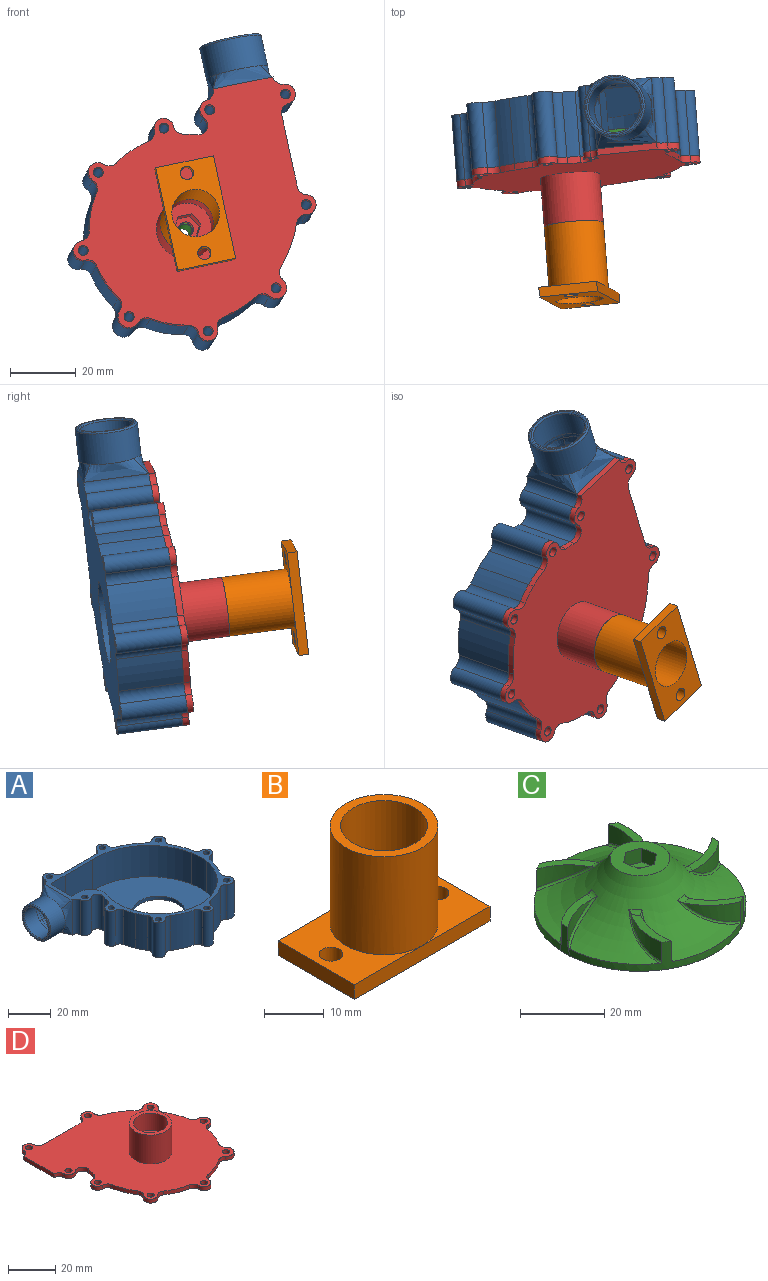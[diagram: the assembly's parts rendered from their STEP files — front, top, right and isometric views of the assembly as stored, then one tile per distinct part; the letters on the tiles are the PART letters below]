
ASSEMBLY  parts=4 mates=3
PART A: 83 faces, bbox 89.8x76.4x20.8 mm
  f0: cylinder r=29.1mm len=20mm, axis (0,0,-1), area 123.2mm2, adj f1,f7,f16,f63
  f1: cylinder r=29.1mm len=20mm, axis (0,0,-1), area 116.2mm2, adj f0,f7,f16,f54
  f2: cylinder r=29.1mm len=20mm, axis (0,0,-1), area 242.2mm2, adj f7,f16,f50,f56
  f3: cylinder r=29.1mm len=20mm, axis (0,0,-1), area 236.9mm2, adj f7,f16,f46,f52
  f4: cylinder r=38.12mm len=20mm, axis (0,0,-1), area 241.8mm2, adj f7,f11,f16,f40
  f5: cylinder r=38.12mm len=20mm, axis (0,0,-1), area 292.6mm2, adj f7,f16,f36,f42
  f6: cylinder r=8.51mm len=18mm, axis (0,0,-1), area 233.2mm2, adj f7,f26,f27,f28,f29,f30
  f7: plane 76.42x75.05mm, normal (0,0,1), area 691.8mm2, adj f0,f1,f2,f3,f4,f5,f6,f8
  f8: cylinder r=29.1mm len=20mm, axis (0,0,-1), area 80mm2, adj f7,f15,f16,f61
  f9: cylinder r=29.1mm len=20mm, axis (0,0,-1), area 235.3mm2, adj f7,f10,f16,f48
  f10: cylinder r=3mm len=20mm, axis (0,0,-1), area 83.6mm2, adj f7,f9,f16,f44
  f11: cylinder r=3mm len=20mm, axis (0,0,-1), area 84.8mm2, adj f4,f7,f16,f44
  f12: cylinder r=38.12mm len=20mm, axis (0,0,-1), area 85.1mm2, adj f7,f13,f16,f38
  f13: plane 20x18.02mm, normal (0,1,0), area 360.4mm2, adj f7,f12,f16,f33
  f14: plane 20x0.02mm, normal (0,-1,0), area 0.4mm2, adj f7,f16,f58,f66
  f15: cylinder r=3mm len=20mm, axis (0,0,-1), area 156mm2, adj f7,f8,f16,f59
  f16: plane 76.42x75.05mm, normal (0,0,-1), area 3092.9mm2, adj f0,f1,f2,f3,f4,f5,f8,f9
  f17: cylinder r=27.1mm len=19.22mm, axis (0,0,-1), area 354mm2, adj f7,f18,f27,f28
  f18: cylinder r=27.1mm len=51.79mm, axis (0,0,-1), area 1258.4mm2, adj f7,f17,f19,f28
  f19: cylinder r=5mm len=18mm, axis (0,0,-1), area 0.8mm2, adj f7,f18,f20,f28
  f20: cylinder r=24.78mm len=18mm, axis (0,0,-1), area 178.9mm2, adj f7,f19,f21,f28
  f21: cylinder r=5mm len=18mm, axis (0,0,-1), area 3.9mm2, adj f7,f20,f22,f28
  f22: cylinder r=36.12mm len=36.86mm, axis (0,0,-1), area 918mm2, adj f7,f21,f23,f28
  f23: plane 18.05x18mm, normal (0,-1,0), area 324.9mm2, adj f7,f22,f24,f28
  f24: plane 18x9.91mm, normal (0.01,-1,0), area 178.4mm2, adj f7,f23,f25,f28
  f25: plane 18x14.36mm, normal (1,0,0), area 29.1mm2, adj f7,f24,f26,f28,f30,f31
  f26: plane 3.82x2mm, normal (-0.08,1,0), area 7.7mm2, adj f6,f7,f25,f30
  f27: cylinder r=5mm len=18mm, axis (0,0,-1), area 7.9mm2, adj f6,f7,f17,f28
  f28: plane 67.53x61.45mm, normal (0,0,1), area 2433mm2, adj f6,f17,f18,f19,f20,f21,f22,f23
  f29: plane 16x9.59mm, normal (0,1,0), area 153.4mm2, adj f6,f28,f30,f73
  f30: plane 14.56x9.59mm, normal (0,0,-1), area 31.9mm2, adj f6,f25,f26,f29,f31,f72
  f31: plane 16x2mm, normal (0,-1,0), area 32mm2, adj f25,f28,f30,f71
  f32: cylinder r=3mm len=20mm, axis (0,0,-1), area 88.8mm2, adj f7,f16,f34,f68
  f33: cylinder r=3mm len=20mm, axis (0,0,-1), area 89.2mm2, adj f7,f13,f16,f34
  f34: cylinder r=3mm len=20mm, axis (0,0,-1), area 179.5mm2, adj f7,f16,f32,f33
  f35: cylinder r=1.5mm len=20mm, axis (0,0,-1), area 188.5mm2, adj f7,f16
  f36: cylinder r=3mm len=20mm, axis (0,0,-1), area 84.2mm2, adj f5,f7,f16,f37
  f37: cylinder r=3mm len=20mm, axis (0,0,-1), area 186mm2, adj f7,f16,f36,f38
  f38: cylinder r=3mm len=20mm, axis (0,0,-1), area 84.2mm2, adj f7,f12,f16,f37
  f39: cylinder r=1.5mm len=20mm, axis (0,0,-1), area 188.5mm2, adj f7,f16
  f40: cylinder r=3mm len=20mm, axis (0,0,-1), area 84.7mm2, adj f4,f7,f16,f41
  f41: cylinder r=3.26mm len=20mm, axis (0,0,-1), area 203.7mm2, adj f7,f16,f40,f42
  f42: cylinder r=3mm len=20mm, axis (0,0,-1), area 84.7mm2, adj f5,f7,f16,f41
  f43: cylinder r=1.5mm len=20mm, axis (0,0,-1), area 188.5mm2, adj f7,f16
  f44: cylinder r=3mm len=20mm, axis (0,0,-1), area 191mm2, adj f7,f10,f11,f16
  f45: cylinder r=1.5mm len=20mm, axis (0,0,-1), area 188.5mm2, adj f7,f16
  f46: cylinder r=3mm len=20mm, axis (0,0,-1), area 83.6mm2, adj f3,f7,f16,f47
  f47: cylinder r=3.38mm len=20mm, axis (0,0,-1), area 215.1mm2, adj f7,f16,f46,f48
  f48: cylinder r=3mm len=20mm, axis (0,0,-1), area 83.6mm2, adj f7,f9,f16,f47
  f49: cylinder r=1.5mm len=20mm, axis (0,0,-1), area 188.5mm2, adj f7,f16
  f50: cylinder r=3mm len=20mm, axis (0,0,-1), area 83.6mm2, adj f2,f7,f16,f51
  f51: cylinder r=3mm len=20mm, axis (0,0,-1), area 189.8mm2, adj f7,f16,f50,f52
  f52: cylinder r=3mm len=20mm, axis (0,0,-1), area 83.6mm2, adj f3,f7,f16,f51
  f53: cylinder r=1.5mm len=20mm, axis (0,0,-1), area 188.5mm2, adj f7,f16
  f54: cylinder r=3mm len=20mm, axis (0,0,-1), area 83.6mm2, adj f1,f7,f16,f55
  f55: cylinder r=3mm len=20mm, axis (0,0,-1), area 189.8mm2, adj f7,f16,f54,f56
  f56: cylinder r=3mm len=20mm, axis (0,0,-1), area 83.6mm2, adj f2,f7,f16,f55
  f57: cylinder r=1.5mm len=20mm, axis (0,0,-1), area 188.5mm2, adj f7,f16
  f58: cylinder r=3mm len=20mm, axis (0,0,-1), area 89.2mm2, adj f7,f14,f16,f59
  f59: cylinder r=3mm len=20mm, axis (0,0,-1), area 131.5mm2, adj f7,f15,f16,f58
  f60: cylinder r=1.5mm len=20mm, axis (0,0,-1), area 188.5mm2, adj f7,f16
  f61: cylinder r=3mm len=20mm, axis (0,0,-1), area 83.6mm2, adj f7,f8,f16,f62
  f62: cylinder r=3mm len=20mm, axis (0,0,-1), area 189.8mm2, adj f7,f16,f61,f63
  f63: cylinder r=3mm len=20mm, axis (0,0,-1), area 83.6mm2, adj f0,f7,f16,f62
  f64: cylinder r=1.5mm len=20mm, axis (0,0,-1), area 188.5mm2, adj f7,f16
  f65: cylinder r=12.5mm len=25mm, axis (0,0,-1), area 157.1mm2, adj f16,f28
  f66: bspline ~20x4.7mm, area 84.7mm2, adj f14,f67,f69,f74
  f67: bspline ~18.52x4.79mm, area 86.6mm2, adj f7,f66,f68,f74
  f68: bspline ~20x4.79mm, area 85.6mm2, adj f32,f67,f69,f74
  f69: bspline ~18.52x4.79mm, area 81.8mm2, adj f16,f66,f68,f74
  f70: bspline ~14.52x4.78mm, area 65.1mm2, adj f28,f71,f73,f79
  f71: bspline ~16x4.78mm, area 69.3mm2, adj f31,f70,f72,f80
  f72: bspline ~14.52x4.78mm, area 66.7mm2, adj f30,f71,f73,f78
  f73: bspline ~16x4.71mm, area 68.3mm2, adj f29,f70,f72,f77
  f74: cylinder r=9.5mm len=19mm, axis (1,0,0), area 567.1mm2, adj f66,f67,f68,f69,f82
  f75: plane 18x18mm, normal (-1,0,0), area 27.5mm2, adj f81,f82
  f76: cylinder r=8mm len=16mm, axis (-1,0,0), area 399mm2, adj f77,f78,f79,f80,f81
  f77: bspline ~12.11x2.96mm, area 20.1mm2, adj f73,f76,f78,f79
  f78: bspline ~12.11x2.96mm, area 20.2mm2, adj f72,f76,f77,f80
  f79: bspline ~12.11x2.96mm, area 20.2mm2, adj f70,f76,f77,f80
  f80: bspline ~12.11x2.96mm, area 20.2mm2, adj f71,f76,f78,f79
  f81: torus R=8.5mm, axis (1,0,0), area 40.4mm2, adj f75,f76
  f82: torus R=9mm, axis (1,0,0), area 46mm2, adj f74,f75
PART B: 12 faces, bbox 32x18x23 mm
  f0: cylinder r=7.25mm len=23mm, axis (0,0,-1), area 1047.7mm2, adj f2,f9
  f1: cylinder r=9mm len=20mm, axis (0,0,-1), area 1131mm2, adj f2,f3,f6
  f2: plane 18x18mm, normal (0,0,1), area 89.3mm2, adj f0,f1
  f3: plane 18x16mm, normal (0,0,1), area 148.2mm2, adj f1,f5,f7,f8,f11
  f4: plane 18x3mm, normal (-1,0,0), area 54mm2, adj f6,f7,f8,f9
  f5: plane 18x3mm, normal (1,0,0), area 54mm2, adj f3,f7,f8,f9
  f6: plane 18x16mm, normal (0,0,1), area 148.2mm2, adj f1,f4,f7,f8,f10
  f7: plane 32x3mm, normal (0,1,0), area 96mm2, adj f3,f4,f5,f6,f9
  f8: plane 32x3mm, normal (0,-1,0), area 96mm2, adj f3,f4,f5,f6,f9
  f9: plane 32x18mm, normal (0,0,-1), area 385.7mm2, adj f0,f4,f5,f7,f8,f10,f11
  f10: cylinder r=2mm len=4mm, axis (0,0,-1), area 37.7mm2, adj f6,f9
  f11: cylinder r=2mm len=4mm, axis (0,0,-1), area 37.7mm2, adj f3,f9
PART C: 48 faces, bbox 61.1x61.1x26.7 mm
  f0: cylinder r=2.1mm len=11mm, axis (0,0,-1), area 145.1mm2, adj f3,f29
  f1: torus R=29.21mm, axis (0,0,-1), area 1865.6mm2, adj f2,f4,f30,f31,f32,f33,f34,f35
  f2: plane 14.2x14.2mm, normal (0,0,1), area 112.2mm2, adj f1,f23,f24,f25,f26,f27,f28
  f3: plane 50.2x50.2mm, normal (0,0,-1), area 1965.4mm2, adj f0,f4
  f4: cylinder r=25.1mm len=50.2mm, axis (0,0,-1), area 400.2mm2, adj f1,f3,f5,f6,f7,f8,f9,f10
  f5: cylinder r=18mm len=12.05mm, axis (0,0,-1), area 35.5mm2, adj f4,f7,f39
  f6: cylinder r=18mm len=13.06mm, axis (0,0,-1), area 49.9mm2, adj f4,f7,f38,f46
  f7: plane 12.88x6.41mm, normal (0,0,1), area 27.6mm2, adj f4,f5,f6,f39,f46
  f8: plane 14.32x4.63mm, normal (0,0,1), area 27.6mm2, adj f4,f9,f10,f37,f45
  f9: cylinder r=18mm len=13.33mm, axis (0,0,-1), area 49.9mm2, adj f4,f8,f36,f45
  f10: cylinder r=18mm len=12.56mm, axis (0,0,-1), area 35.5mm2, adj f4,f8,f37
  f11: plane 12.88x6.41mm, normal (0,0,1), area 27.6mm2, adj f4,f12,f13,f33,f43
  f12: cylinder r=18mm len=12.05mm, axis (0,0,-1), area 35.5mm2, adj f4,f11,f33
  f13: cylinder r=18mm len=13.06mm, axis (0,0,-1), area 49.9mm2, adj f4,f11,f32,f43
  f14: cylinder r=18mm len=13.33mm, axis (0,0,-1), area 49.9mm2, adj f4,f16,f30,f42
  f15: cylinder r=18mm len=12.56mm, axis (0,0,-1), area 35.5mm2, adj f4,f16,f31
  f16: plane 14.32x4.63mm, normal (0,0,1), area 27.6mm2, adj f4,f14,f15,f31,f42
  f17: cylinder r=18mm len=10.03mm, axis (0,0,-1), area 49.9mm2, adj f4,f19,f34,f44
  f18: cylinder r=18mm len=9.7mm, axis (0,0,-1), area 35.5mm2, adj f4,f19,f35
  f19: plane 11.94x9.52mm, normal (0,0,1), area 27.6mm2, adj f4,f17,f18,f35,f44
  f20: cylinder r=18mm len=9.7mm, axis (0,0,-1), area 35.5mm2, adj f4,f22,f40
  f21: cylinder r=18mm len=10.03mm, axis (0,0,-1), area 49.9mm2, adj f4,f22,f41,f47
  f22: plane 11.94x9.52mm, normal (0,0,1), area 27.6mm2, adj f4,f20,f21,f40,f47
  f23: plane 4x3.93mm, normal (0.36,0.93,0), area 16.9mm2, adj f2,f24,f28,f29
  f24: plane 4x3.28mm, normal (-0.63,0.78,0), area 16.9mm2, adj f2,f23,f25,f29
  f25: plane 4.16x4mm, normal (-0.99,-0.15,0), area 16.9mm2, adj f2,f24,f26,f29
  f26: plane 4x3.93mm, normal (-0.36,-0.93,0), area 16.9mm2, adj f2,f25,f27,f29
  f27: plane 4x3.28mm, normal (0.63,-0.78,0), area 16.9mm2, adj f2,f26,f28,f29
  f28: plane 4.16x4mm, normal (0.99,0.15,0), area 16.9mm2, adj f2,f23,f27,f29
  f29: plane 8.33x7.86mm, normal (0,0,1), area 32.3mm2, adj f0,f23,f24,f25,f26,f27,f28
  f30: bspline ~17.28x8.18mm, area 11mm2, adj f1,f4,f14,f42
  f31: bspline ~16.64x8.2mm, area 13.1mm2, adj f1,f4,f15,f16,f42
  f32: bspline ~16.34x8.08mm, area 11mm2, adj f1,f4,f13,f43
  f33: bspline ~16.1x8.2mm, area 13.1mm2, adj f1,f4,f11,f12,f43
  f34: bspline ~12.58x12.41mm, area 11mm2, adj f1,f4,f17,f44
  f35: bspline ~12.7x10.93mm, area 13.1mm2, adj f1,f4,f18,f19,f44
  f36: bspline ~17.28x8.18mm, area 11mm2, adj f1,f4,f9,f45
  f37: bspline ~16.64x8.2mm, area 13.1mm2, adj f1,f4,f8,f10,f45
  f38: bspline ~16.34x8.08mm, area 11mm2, adj f1,f4,f6,f46
  f39: bspline ~16.1x8.2mm, area 13.1mm2, adj f1,f4,f5,f7,f46
  f40: bspline ~12.7x10.93mm, area 13.1mm2, adj f1,f4,f20,f22,f47
  f41: bspline ~12.58x12.41mm, area 11mm2, adj f1,f4,f21,f47
  f42: torus R=13.36mm, axis (0,0,1), area 4mm2, adj f1,f14,f16,f30,f31
  f43: torus R=13.36mm, axis (0,0,1), area 4mm2, adj f1,f11,f13,f32,f33
  f44: torus R=13.36mm, axis (0,0,1), area 4mm2, adj f1,f17,f19,f34,f35
  f45: torus R=13.36mm, axis (0,0,1), area 4mm2, adj f1,f8,f9,f36,f37
  f46: torus R=13.36mm, axis (0,0,1), area 4mm2, adj f1,f6,f7,f38,f39
  f47: torus R=13.36mm, axis (0,0,1), area 4mm2, adj f1,f21,f22,f40,f41
PART D: 62 faces, bbox 75.1x76.4x17 mm
  f0: cylinder r=2.25mm len=4.5mm, axis (0,0,1), area 28.3mm2, adj f50,f61
  f1: cylinder r=29.1mm len=5.89mm, axis (0,0,-1), area 12.3mm2, adj f2,f47,f49,f50
  f2: cylinder r=29.1mm len=5.13mm, axis (0,0,-1), area 11.6mm2, adj f1,f3,f49,f50
  f3: cylinder r=3mm len=3.83mm, axis (0,0,-1), area 8.4mm2, adj f2,f4,f49,f50
  f4: cylinder r=3mm len=5.17mm, axis (0,0,-1), area 19mm2, adj f3,f5,f49,f50
  f5: cylinder r=3mm len=3.84mm, axis (0,0,-1), area 8.4mm2, adj f4,f6,f49,f50
  f6: cylinder r=29.1mm len=11.07mm, axis (0,0,-1), area 24.2mm2, adj f5,f7,f49,f50
  f7: cylinder r=3mm len=2.99mm, axis (0,0,-1), area 8.4mm2, adj f6,f8,f49,f50
  f8: cylinder r=3mm len=6mm, axis (0,0,-1), area 19mm2, adj f7,f9,f49,f50
  f9: cylinder r=3mm len=2.97mm, axis (0,0,-1), area 8.4mm2, adj f8,f10,f49,f50
  f10: cylinder r=29.1mm len=10.9mm, axis (0,0,-1), area 23.7mm2, adj f9,f11,f49,f50
  f11: cylinder r=3mm len=3.83mm, axis (0,0,-1), area 8.4mm2, adj f10,f12,f49,f50
  f12: cylinder r=3.38mm len=5.83mm, axis (0,0,-1), area 21.5mm2, adj f11,f13,f49,f50
  f13: cylinder r=3mm len=3.82mm, axis (0,0,-1), area 8.4mm2, adj f12,f14,f49,f50
  f14: cylinder r=29.1mm len=10.86mm, axis (0,0,-1), area 23.5mm2, adj f13,f15,f49,f50
  f15: cylinder r=3mm len=2.95mm, axis (0,0,-1), area 8.4mm2, adj f14,f16,f49,f50
  f16: cylinder r=3mm len=6mm, axis (0,0,-1), area 19.1mm2, adj f15,f17,f49,f50
  f17: cylinder r=3mm len=3.07mm, axis (0,0,-1), area 8.5mm2, adj f16,f18,f49,f50
  f18: cylinder r=38.12mm len=11.28mm, axis (0,0,-1), area 24.2mm2, adj f17,f19,f49,f50
  f19: cylinder r=3mm len=3.82mm, axis (0,0,-1), area 8.5mm2, adj f18,f20,f49,f50
  f20: cylinder r=3.26mm len=5.8mm, axis (0,0,-1), area 20.4mm2, adj f19,f21,f49,f50
  f21: cylinder r=3mm len=3.89mm, axis (0,0,-1), area 8.5mm2, adj f20,f22,f49,f50
  f22: cylinder r=38.12mm len=12.34mm, axis (0,0,-1), area 29.3mm2, adj f21,f23,f49,f50
  f23: cylinder r=3mm len=3.39mm, axis (0,0,-1), area 8.4mm2, adj f22,f24,f49,f50
  f24: cylinder r=3mm len=5.91mm, axis (0,0,-1), area 18.6mm2, adj f23,f25,f49,f50
  f25: cylinder r=3mm len=3.13mm, axis (0,0,-1), area 8.4mm2, adj f24,f26,f49,f50
  f26: cylinder r=38.12mm len=4.25mm, axis (0,0,-1), area 8.5mm2, adj f25,f27,f49,f50
  f27: plane 18.02x2mm, normal (0,1,0), area 36mm2, adj f26,f28,f49,f50
  f28: cylinder r=3mm len=2.99mm, axis (0,0,-1), area 8.9mm2, adj f27,f29,f49,f50
  f29: cylinder r=3mm len=5.98mm, axis (0,0,-1), area 18mm2, adj f28,f30,f49,f50
  f30: cylinder r=3mm len=2.92mm, axis (0,0,-1), area 8.9mm2, adj f29,f31,f49,f50
  f31: plane 18.52x2mm, normal (-1,0,0), area 37mm2, adj f30,f32,f49,f50
  f32: plane 2x0.02mm, normal (0,-1,0), area 0mm2, adj f31,f33,f49,f50
  f33: cylinder r=3mm len=2.99mm, axis (0,0,-1), area 8.9mm2, adj f32,f34,f49,f50
  f34: cylinder r=3mm len=4.93mm, axis (0,0,-1), area 13.1mm2, adj f33,f35,f49,f50
  f35: cylinder r=3mm len=4.94mm, axis (0,0,-1), area 15.6mm2, adj f34,f36,f49,f50
  f36: cylinder r=29.1mm len=3.87mm, axis (0,0,-1), area 8mm2, adj f35,f37,f49,f50
  f37: cylinder r=3mm len=2.98mm, axis (0,0,-1), area 8.4mm2, adj f36,f38,f49,f50
  f38: cylinder r=3mm len=6mm, axis (0,0,-1), area 19mm2, adj f37,f47,f49,f50
  f39: cylinder r=1.5mm len=3mm, axis (0,0,-1), area 18.8mm2, adj f49,f50
  f40: cylinder r=1.5mm len=3mm, axis (0,0,-1), area 18.8mm2, adj f49,f50
  f41: cylinder r=1.5mm len=3mm, axis (0,0,-1), area 18.8mm2, adj f49,f50
  f42: cylinder r=1.5mm len=3mm, axis (0,0,-1), area 18.8mm2, adj f49,f50
  f43: cylinder r=1.5mm len=3mm, axis (0,0,-1), area 18.8mm2, adj f49,f50
  f44: cylinder r=1.5mm len=3mm, axis (0,0,-1), area 18.8mm2, adj f49,f50
  f45: cylinder r=1.5mm len=3mm, axis (0,0,-1), area 18.8mm2, adj f49,f50
  f46: cylinder r=1.5mm len=3mm, axis (0,0,-1), area 18.8mm2, adj f49,f50
  f47: cylinder r=3mm len=2.98mm, axis (0,0,-1), area 8.4mm2, adj f1,f38,f49,f50
  f48: cylinder r=1.5mm len=3mm, axis (0,0,-1), area 18.8mm2, adj f49,f50
  f49: plane 76.42x75.05mm, normal (0,0,1), area 3329.3mm2, adj f1,f2,f3,f4,f5,f6,f7,f8
  f50: plane 76.42x75.05mm, normal (0,0,-1), area 3567.9mm2, adj f0,f1,f2,f3,f4,f5,f6,f7
  f51: cylinder r=7.25mm len=14.5mm, axis (0,0,-1), area 410mm2, adj f53,f54
  f52: cylinder r=9mm len=18mm, axis (0,0,-1), area 848.2mm2, adj f49,f53
  f53: plane 18x18mm, normal (0,0,1), area 89.3mm2, adj f51,f52
  f54: plane 14.5x14.5mm, normal (0,0,1), area 120.2mm2, adj f51,f55,f56,f57,f58,f59,f60
  f55: plane 6x3.62mm, normal (0.49,0.87,0), area 24.9mm2, adj f54,f56,f60,f61
  f56: plane 6x3.58mm, normal (-0.51,0.86,0), area 24.9mm2, adj f54,f55,f57,f61
  f57: plane 6x4.16mm, normal (-1,-0.01,0), area 24.9mm2, adj f54,f56,f58,f61
  f58: plane 6x3.62mm, normal (-0.49,-0.87,0), area 24.9mm2, adj f54,f57,f59,f61
  f59: plane 6x3.58mm, normal (0.51,-0.86,0), area 24.9mm2, adj f54,f58,f60,f61
  f60: plane 6x4.16mm, normal (1,0.01,0), area 24.9mm2, adj f54,f55,f59,f61
  f61: plane 8.31x7.23mm, normal (0,0,1), area 29mm2, adj f0,f55,f56,f57,f58,f59,f60
PLACE A rot(axis=(0.62,0.55,-0.57),106.1deg) t=(-2.72,47.28,13.26)mm
PLACE B rot(axis=(-0.69,0.52,0.5),120.7deg) t=(1.91,-12.03,21.07)mm
PLACE C rot(axis=(-0.89,0.32,0.34),106deg) t=(-2.58,45.43,13.51)mm
PLACE D rot(axis=(0.62,0.55,-0.57),106.1deg) t=(-1.18,27.51,15.87)mm
MATE revolute C.f0 <-> A.f65  axis (-0.08,0.99,-0.13) through (-2.49,44.31,13.65)mm
MATE fastened B.f1 <-> D.f51  axis (-0.08,0.99,-0.13) through (0.13,10.71,18.08)mm
MATE fastened D.f50 <-> A.f7  axis (-0.08,0.99,-0.13) through (16.21,34.72,60.29)mm
